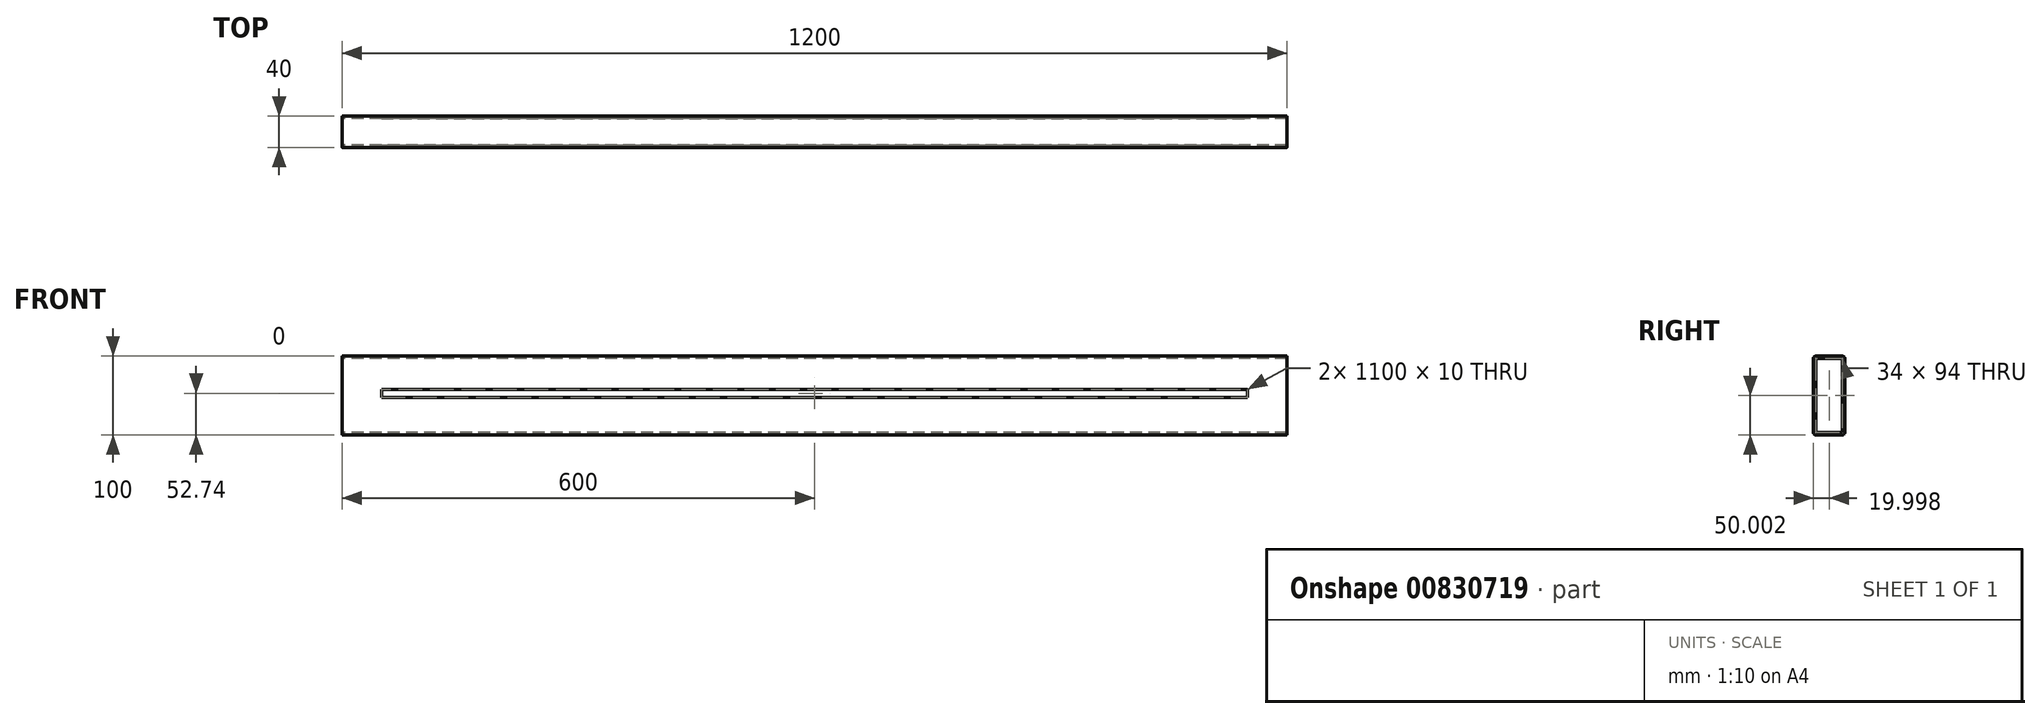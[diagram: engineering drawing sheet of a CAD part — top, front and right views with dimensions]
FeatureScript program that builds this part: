
annotation { "Feature Type Name" : "Feature", "Feature Type Description" : "" }
export const myFeature = defineFeature(function(context is Context, id is Id, definition is map)
    precondition{}
    {
        {
            assignVariable(context, id + "F0", {"name" : "LongSideSize", "anyValue" : 1200});
        }
        {
            var Q0;
            Q0=qCreatedBy(makeId("Right.planeOp"),FACE);
            var sketch = newSketch(context, id + "F1", { "sketchPlane" : qUnion([Q0])});
            skPoint(sketch, "E0.middle", {"position": v(-14.96, 34.76) * mm});
            skLineSegment(sketch, "E1.bottom", {"start": v(-16.25, -52.74) * mm, "end": v(17.75, -52.74) * mm});
            skLineSegment(sketch, "E1.top", {"start": v(-16.25, 47.26) * mm, "end": v(17.75, 47.26) * mm});
            skLineSegment(sketch, "E1.left", {"start": v(-19.25, -49.74) * mm, "end": v(-19.25, 44.26) * mm});
            skLineSegment(sketch, "E1.right", {"start": v(20.75, -49.74) * mm, "end": v(20.75, 44.26) * mm});
            skPoint(sketch, "E2.visualSharp", {"position": v(-19.25, 47.26) * mm});
            skArc(sketch, "E2.filletArc", {"start": v(-16.25, 47.26) * mm, "mid": v(-18.37, 46.38) * mm, "end": v(-19.25, 44.26) * mm});
            skPoint(sketch, "E3.visualSharp", {"position": v(20.75, 47.26) * mm});
            skArc(sketch, "E3.filletArc", {"start": v(20.75, 44.26) * mm, "mid": v(19.87, 46.38) * mm, "end": v(17.75, 47.26) * mm});
            skPoint(sketch, "E4.visualSharp", {"position": v(20.75, -52.74) * mm});
            skArc(sketch, "E4.filletArc", {"start": v(17.75, -52.74) * mm, "mid": v(19.87, -51.86) * mm, "end": v(20.75, -49.74) * mm});
            skPoint(sketch, "E5.visualSharp", {"position": v(-19.25, -52.74) * mm});
            skArc(sketch, "E5.filletArc", {"start": v(-19.25, -49.74) * mm, "mid": v(-18.37, -51.86) * mm, "end": v(-16.25, -52.74) * mm});
            skLineSegment(sketch, "E6.0", {"start": v(-17.25, 46.26) * mm, "end": v(-17.25, 46.26) * mm});
            skLineSegment(sketch, "E6.2", {"start": v(-17.25, -49.74) * mm, "end": v(-17.25, -49.74) * mm});
            skLineSegment(sketch, "E6.4", {"start": v(18.75, -49.74) * mm, "end": v(18.75, -49.74) * mm});
            skLineSegment(sketch, "E6.7", {"start": v(18.75, 46.26) * mm, "end": v(18.75, 46.26) * mm});
            skLineSegment(sketch, "E7.0", {"start": v(17.75, -49.74) * mm, "end": v(17.75, 44.26) * mm});
            skLineSegment(sketch, "E7.1", {"start": v(-16.25, -49.74) * mm, "end": v(17.75, -49.74) * mm});
            skLineSegment(sketch, "E7.2", {"start": v(-16.25, -49.74) * mm, "end": v(-16.25, 44.26) * mm});
            skLineSegment(sketch, "E7.3", {"start": v(-16.25, 44.26) * mm, "end": v(17.75, 44.26) * mm});
            skSolve(sketch);
        }
        {
            var Q0;
            Q0=qSketchRegion(id+"F1",true);
            extrude(context, id + "F2", {"entities" : qUnion([Q0]), "endBound" : BoundingType.SYMMETRIC, "depth" : (getVariable(context, 'LongSideSize')) * mm, "offsetDistance" : 25 * mm});
        }
        {
            var Q0;
            Q0=makeQuery(id+"F2.opExtrude","SWEPT_BODY",BODY,{"disambiguationData":[OSD([sQuery(id+"F1.wireOp",EDGE,"E1.bottom"),sQuery(id+"F1.wireOp",EDGE,"E1.top"),sQuery(id+"F1.wireOp",EDGE,"E1.left"),sQuery(id+"F1.wireOp",EDGE,"E1.right"),sQuery(id+"F1.wireOp",EDGE,"E2.filletArc"),sQuery(id+"F1.wireOp",EDGE,"E3.filletArc"),sQuery(id+"F1.wireOp",EDGE,"E4.filletArc"),sQuery(id+"F1.wireOp",EDGE,"E5.filletArc"),sQuery(id+"F1.wireOp",EDGE,"E7.0"),sQuery(id+"F1.wireOp",EDGE,"E7.1"),sQuery(id+"F1.wireOp",EDGE,"E7.2"),sQuery(id+"F1.wireOp",EDGE,"E7.3")])]});
            transform(context, id + "F3", {"entities" : qUnion([Q0]), "transformType" : TransformType.TRANSLATION_3D, "dx" : 0 * mm, "dy" : 0 * mm, "dz" : 0 * mm, "makeCopy" : true});
        }
        {
            var Q0;
            Q0=makeQuery(id+"F3.opPattern","COPY",BODY,{"derivedFrom":makeQuery(id+"F2.opExtrude","SWEPT_BODY",BODY,{"disambiguationData":[OSD([sQuery(id+"F1.wireOp",EDGE,"E1.bottom"),sQuery(id+"F1.wireOp",EDGE,"E1.top"),sQuery(id+"F1.wireOp",EDGE,"E1.left"),sQuery(id+"F1.wireOp",EDGE,"E1.right"),sQuery(id+"F1.wireOp",EDGE,"E2.filletArc"),sQuery(id+"F1.wireOp",EDGE,"E3.filletArc"),sQuery(id+"F1.wireOp",EDGE,"E4.filletArc"),sQuery(id+"F1.wireOp",EDGE,"E5.filletArc"),sQuery(id+"F1.wireOp",EDGE,"E7.0"),sQuery(id+"F1.wireOp",EDGE,"E7.1"),sQuery(id+"F1.wireOp",EDGE,"E7.2"),sQuery(id+"F1.wireOp",EDGE,"E7.3")])]}),"instanceName":"1"});
            deleteBodies(context, id + "F4", {"entities" : qUnion([Q0])});
        }
        {
            var Q0;
            Q0=makeQuery(id+"F2.opExtrude","SWEPT_FACE",FACE,{"disambiguationData":[OSD([sQuery(id+"F1.wireOp",EDGE,"E1.left")])]});
            var sketch = newSketch(context, id + "F5", { "sketchPlane" : qUnion([Q0])});
            skLineSegment(sketch, "E8.bottom", {"start": v(-550, -5) * mm, "end": v(550, -5) * mm});
            skLineSegment(sketch, "E8.top", {"start": v(-550, 5) * mm, "end": v(550, 5) * mm});
            skLineSegment(sketch, "E8.left", {"start": v(-550, -5) * mm, "end": v(-550, 5) * mm});
            skLineSegment(sketch, "E8.right", {"start": v(550, -5) * mm, "end": v(550, 5) * mm});
            skPoint(sketch, "E8.middle", {"position": v(0, 0) * mm});
            skSolve(sketch);
        }
        {
            var Q0;
            Q0=makeQuery(id+"F5.imprint","IMPRINT",FACE,{"disambiguationData":[TD([[makeQuery(id+"F5.imprint","IMPRINT",EDGE,{"derivedFrom":sQuery(id+"F5.wireOp",EDGE,"E8.bottom")}),1.0]])]});
            extrude(context, id + "F6", {"entities" : qUnion([Q0]), "operationType" : NewBodyOperationType.REMOVE, "endBound" : BoundingType.THROUGH_ALL, "oppositeDirection" : true, "depth" : 25 * mm, "offsetDistance" : 25 * mm});
        }
    });
